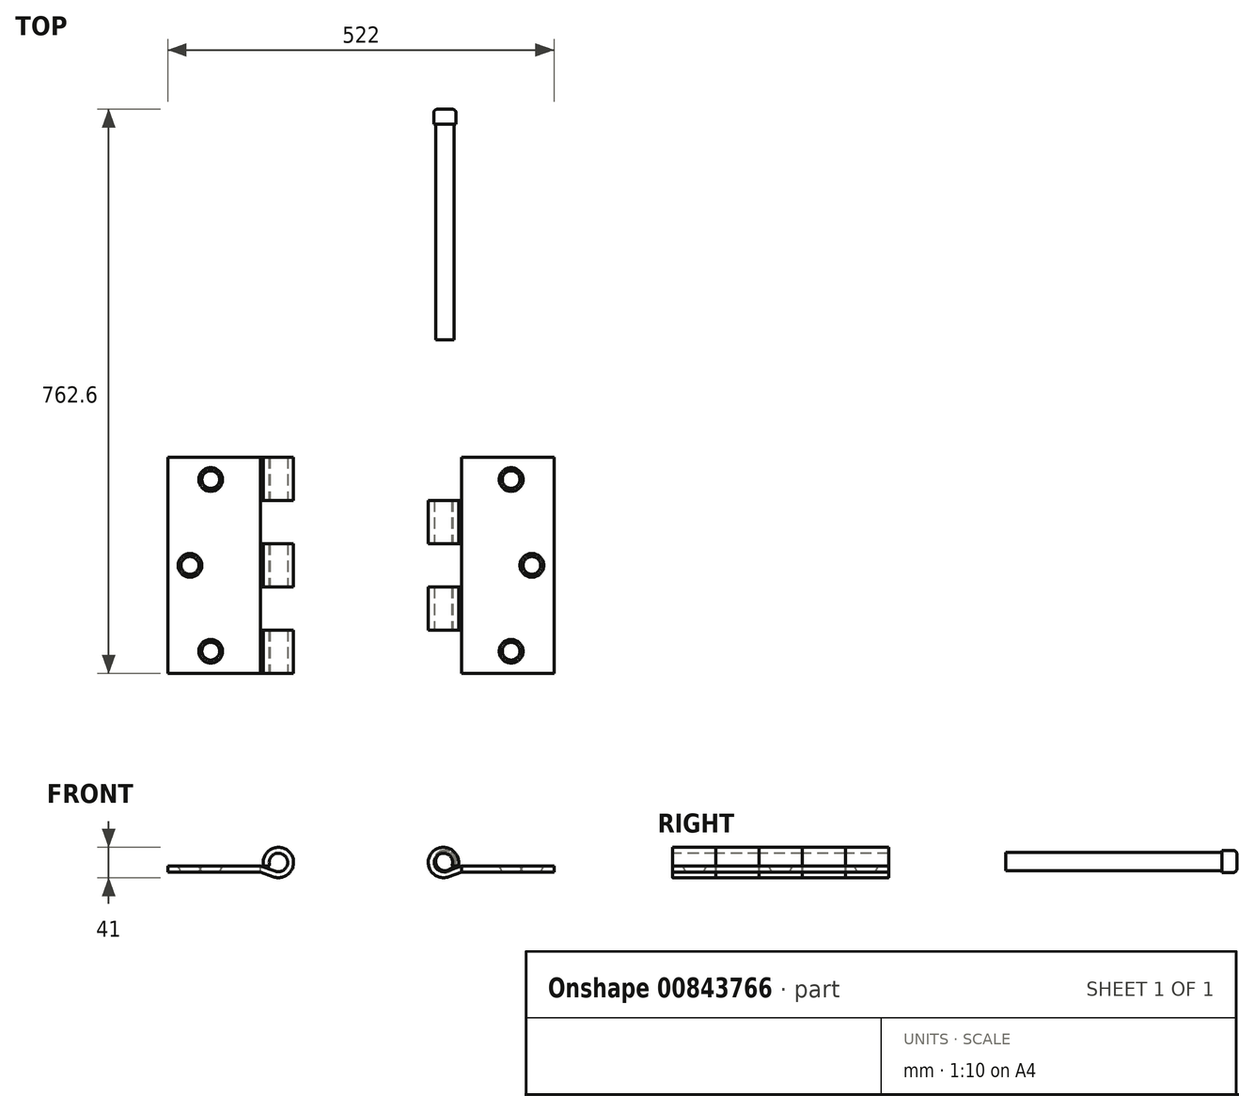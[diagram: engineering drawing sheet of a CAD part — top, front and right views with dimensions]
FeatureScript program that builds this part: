
annotation { "Feature Type Name" : "Feature", "Feature Type Description" : "" }
export const myFeature = defineFeature(function(context is Context, id is Id, definition is map)
    precondition{}
    {
        {
            var Q0;
            Q0=qCreatedBy(makeId("Top.planeOp"),FACE);
            var sketch = newSketch(context, id + "F0", { "sketchPlane" : qUnion([Q0])});
            skLineSegment(sketch, "E0.bottom", {"start": v(62.5, -146) * mm, "end": v(-62.5, -146) * mm});
            skLineSegment(sketch, "E0.top", {"start": v(62.5, 146) * mm, "end": v(-62.5, 146) * mm});
            skLineSegment(sketch, "E0.left", {"start": v(62.5, -146) * mm, "end": v(62.5, 146) * mm});
            skLineSegment(sketch, "E0.right", {"start": v(-62.5, -146) * mm, "end": v(-62.5, 146) * mm});
            skPoint(sketch, "E0.middle", {"position": v(0, 0) * mm});
            skLineSegment(sketch, "E1.bottom", {"start": v(62.5, 146) * mm, "end": v(4.5, 146) * mm});
            skLineSegment(sketch, "E1.left", {"start": v(62.5, 146) * mm, "end": v(62.5, 116) * mm});
            skLineSegment(sketch, "E2.bottom", {"start": v(62.5, -146) * mm, "end": v(4.5, -146) * mm});
            skSolve(sketch);
        }
        {
            var Q0;
            Q0=makeQuery(id+"F0.imprint","IMPRINT",FACE,{"disambiguationData":[TD([[makeQuery(id+"F0.imprint","IMPRINT",EDGE,{"derivedFrom":sQuery(id+"F0.wireOp",EDGE,"E0.bottom")}),-1.0]])]});
            extrude(context, id + "F1", {"entities" : qUnion([Q0]), "depth" : 8 * mm, "offsetDistance" : 25 * mm});
        }
        {
            var Q0;
            Q0=makeQuery(id+"F1.opExtrude","SWEPT_FACE",FACE,{"disambiguationData":[OSD([sQuery(id+"F0.wireOp",EDGE,"E0.right")])]});
            cPlane(context, id + "F2", {"entities" : qUnion([Q0]), "cplaneType" : CPlaneType.OFFSET, "offset" : 136 * mm, "width" : 150 * mm, "height" : 150 * mm});
        }
        {
            var Q0;
            Q0=makeQuery(id+"F1.opExtrude","SWEPT_FACE",FACE,{"disambiguationData":[OSD([sQuery(id+"F0.wireOp",EDGE,"E0.bottom"),sQuery(id+"F0.wireOp",EDGE,"E2.bottom")])]});
            var sketch = newSketch(context, id + "F3", { "sketchPlane" : qUnion([Q0])});
            skArc(sketch, "E3", {"start": v(-75.54, 8) * mm, "mid": v(-95.44, 22.22) * mm, "end": v(-83.04, 1.14) * mm});
            skArc(sketch, "E4", {"start": v(-67.12, 8) * mm, "mid": v(-102.19, 26.77) * mm, "end": v(-80.09, -6.3) * mm});
            skLineSegment(sketch, "E5", {"start": v(-62.5, 0) * mm, "end": v(-80.09, -6.3) * mm});
            skLineSegment(sketch, "E6", {"start": v(-62.5, 8) * mm, "end": v(-83.04, 1.14) * mm});
            skLineSegment(sketch, "E7", {"start": v(-67.12, 8) * mm, "end": v(-75.54, 8) * mm});
            skSolve(sketch);
        }
        {
            var Q0;
            Q0=makeQuery(id+"F3.imprint","IMPRINT",FACE,{"disambiguationData":[TD([[makeQuery(id+"F3.imprint","IMPRINT",EDGE,{"derivedFrom":sQuery(id+"F3.wireOp",EDGE,"E3")}),-1.0]])]});
            extrude(context, id + "F4", {"entities" : qUnion([Q0]), "operationType" : NewBodyOperationType.ADD, "oppositeDirection" : true, "depth" : 292 * mm, "offsetDistance" : 25 * mm});
        }
        {
            var Q0;
            Q0=makeQuery(id+"F1.opExtrude","CAP_FACE",FACE,{"disambiguationData":[OSD([sQuery(id+"F0.wireOp",EDGE,"E0.bottom"),sQuery(id+"F0.wireOp",EDGE,"E0.top"),sQuery(id+"F0.wireOp",EDGE,"E0.left"),sQuery(id+"F0.wireOp",EDGE,"E0.right"),sQuery(id+"F0.wireOp",EDGE,"E1.bottom"),sQuery(id+"F0.wireOp",EDGE,"E1.left"),sQuery(id+"F0.wireOp",EDGE,"E2.bottom")])],"isStart":false});
            var sketch = newSketch(context, id + "F5", { "sketchPlane" : qUnion([Q0])});
            skPoint(sketch, "E8.orphan", {"position": v(62.5, 0) * mm});
            skCircle(sketch, "E9", {"center": v(4.5, 116) * mm, "radius": 16 * mm});
            skCircle(sketch, "E10", {"center": v(32.5, 0) * mm, "radius": 16 * mm});
            skCircle(sketch, "E11", {"center": v(4.5, -116) * mm, "radius": 16 * mm});
            skSolve(sketch);
        }
        {
            var Q0;
            Q0=makeQuery(id+"F0.imprint","IMPRINT",FACE,{"disambiguationData":[TD([[makeQuery(id+"F0.imprint","IMPRINT",EDGE,{"derivedFrom":sQuery(id+"F0.wireOp",EDGE,"E0.bottom")}),-1.0]])]});
            var sketch = newSketch(context, id + "F6", { "sketchPlane" : qUnion([Q0])});
            skPoint(sketch, "E12.0", {"position": v(4.5, -116) * mm});
            skPoint(sketch, "E13.0", {"position": v(32.5, 0) * mm});
            skPoint(sketch, "E14.0", {"position": v(4.5, 116) * mm});
            skCircle(sketch, "E15", {"center": v(32.5, 0) * mm, "radius": 12 * mm});
            skCircle(sketch, "E16", {"center": v(4.5, -116) * mm, "radius": 12 * mm});
            skCircle(sketch, "E17", {"center": v(4.5, 116) * mm, "radius": 12 * mm});
            skSolve(sketch);
        }
        {
            var Q0;
            Q0=makeQuery(id+"F1.opExtrude","CAP_FACE",FACE,{"disambiguationData":[OSD([sQuery(id+"F0.wireOp",EDGE,"E0.bottom"),sQuery(id+"F0.wireOp",EDGE,"E0.top"),sQuery(id+"F0.wireOp",EDGE,"E0.left"),sQuery(id+"F0.wireOp",EDGE,"E0.right"),sQuery(id+"F0.wireOp",EDGE,"E1.bottom"),sQuery(id+"F0.wireOp",EDGE,"E1.left"),sQuery(id+"F0.wireOp",EDGE,"E2.bottom")])],"isStart":false});
            var sketch = newSketch(context, id + "F7", { "sketchPlane" : qUnion([Q0])});
            skLineSegment(sketch, "E18.bottom", {"start": v(-62.5, 146) * mm, "end": v(-181.75, 146) * mm});
            skLineSegment(sketch, "E18.top", {"start": v(-62.5, 87.6) * mm, "end": v(-181.75, 87.6) * mm});
            skLineSegment(sketch, "E18.left", {"start": v(-62.5, 146) * mm, "end": v(-62.5, 87.6) * mm});
            skLineSegment(sketch, "E18.right", {"start": v(-181.75, 146) * mm, "end": v(-181.75, 87.6) * mm});
            skLineSegment(sketch, "E19.bottom", {"start": v(-62.5, 29.2) * mm, "end": v(-181.75, 29.2) * mm});
            skLineSegment(sketch, "E19.top", {"start": v(-62.5, -29.2) * mm, "end": v(-181.75, -29.2) * mm});
            skLineSegment(sketch, "E19.left", {"start": v(-62.5, 29.2) * mm, "end": v(-62.5, -29.2) * mm});
            skLineSegment(sketch, "E19.right", {"start": v(-181.75, 29.2) * mm, "end": v(-181.75, -29.2) * mm});
            skLineSegment(sketch, "E20.bottom", {"start": v(-62.5, -87.6) * mm, "end": v(-181.74, -87.6) * mm});
            skLineSegment(sketch, "E20.top", {"start": v(-62.5, -146) * mm, "end": v(-181.74, -146) * mm});
            skLineSegment(sketch, "E20.left", {"start": v(-62.5, -87.6) * mm, "end": v(-62.5, -146) * mm});
            skLineSegment(sketch, "E20.right", {"start": v(-181.74, -87.6) * mm, "end": v(-181.74, -146) * mm});
            skSolve(sketch);
        }
        {
            var Q1;
            Q1=makeQuery(id+"F6.imprint","IMPRINT",FACE,{"disambiguationData":[TD([[makeQuery(id+"F6.imprint","IMPRINT",EDGE,{"derivedFrom":sQuery(id+"F6.wireOp",EDGE,"E16")}),1.0]])]});
            var Q2;
            Q2=makeQuery(id+"F5.imprint","IMPRINT",FACE,{"disambiguationData":[TD([[makeQuery(id+"F5.imprint","IMPRINT",EDGE,{"derivedFrom":sQuery(id+"F5.wireOp",EDGE,"E11")}),1.0]])]});
            loft(context, id + "F8", {"operationType" : NewBodyOperationType.REMOVE, "sheetProfilesArray" : [{ "sheetProfileEntities" : qUnion([Q1]) }, { "sheetProfileEntities" : qUnion([Q2]) }]});
        }
        {
            var Q1;
            Q1=makeQuery(id+"F6.imprint","IMPRINT",FACE,{"disambiguationData":[TD([[makeQuery(id+"F6.imprint","IMPRINT",EDGE,{"derivedFrom":sQuery(id+"F6.wireOp",EDGE,"E15")}),1.0]])]});
            var Q2;
            Q2=makeQuery(id+"F5.imprint","IMPRINT",FACE,{"disambiguationData":[TD([[makeQuery(id+"F5.imprint","IMPRINT",EDGE,{"derivedFrom":sQuery(id+"F5.wireOp",EDGE,"E10")}),1.0]])]});
            loft(context, id + "F9", {"operationType" : NewBodyOperationType.REMOVE, "sheetProfilesArray" : [{ "sheetProfileEntities" : qUnion([Q1]) }, { "sheetProfileEntities" : qUnion([Q2]) }]});
        }
        {
            var Q1;
            Q1=makeQuery(id+"F5.imprint","IMPRINT",FACE,{"disambiguationData":[TD([[makeQuery(id+"F5.imprint","IMPRINT",EDGE,{"derivedFrom":sQuery(id+"F5.wireOp",EDGE,"E9")}),1.0]])]});
            var Q2;
            Q2=makeQuery(id+"F6.imprint","IMPRINT",FACE,{"disambiguationData":[TD([[makeQuery(id+"F6.imprint","IMPRINT",EDGE,{"derivedFrom":sQuery(id+"F6.wireOp",EDGE,"E17")}),1.0]])]});
            loft(context, id + "F10", {"operationType" : NewBodyOperationType.REMOVE, "sheetProfilesArray" : [{ "sheetProfileEntities" : qUnion([Q1]) }, { "sheetProfileEntities" : qUnion([Q2]) }]});
        }
        {
            var Q0;
            Q0=makeQuery(id+"F1.opExtrude","SWEPT_BODY",BODY,{"disambiguationData":[OSD([sQuery(id+"F0.wireOp",EDGE,"E0.bottom"),sQuery(id+"F0.wireOp",EDGE,"E0.top"),sQuery(id+"F0.wireOp",EDGE,"E0.left"),sQuery(id+"F0.wireOp",EDGE,"E0.right"),sQuery(id+"F0.wireOp",EDGE,"E1.bottom"),sQuery(id+"F0.wireOp",EDGE,"E1.left"),sQuery(id+"F0.wireOp",EDGE,"E2.bottom")])]});
            var Q1;
            Q1=qCreatedBy(id+"F2.planeOp",FACE);
            mirror(context, id + "F11", {"entities" : qUnion([Q0]), "mirrorPlane" : qUnion([Q1])});
        }
        {
            var Q0;
            Q0=makeQuery(id+"F11.opPattern","COPY",FACE,{"derivedFrom":makeQuery(id+"F1.opExtrude","CAP_FACE",FACE,{"disambiguationData":[OSD([sQuery(id+"F0.wireOp",EDGE,"E0.bottom"),sQuery(id+"F0.wireOp",EDGE,"E0.top"),sQuery(id+"F0.wireOp",EDGE,"E0.left"),sQuery(id+"F0.wireOp",EDGE,"E0.right"),sQuery(id+"F0.wireOp",EDGE,"E1.bottom"),sQuery(id+"F0.wireOp",EDGE,"E1.left"),sQuery(id+"F0.wireOp",EDGE,"E2.bottom")])],"isStart":false}),"instanceName":"1"});
            var sketch = newSketch(context, id + "F12", { "sketchPlane" : qUnion([Q0])});
            skLineSegment(sketch, "E21.bottom", {"start": v(-334.5, -87.6) * mm, "end": v(-219.8, -87.6) * mm});
            skLineSegment(sketch, "E21.top", {"start": v(-334.5, -29.2) * mm, "end": v(-219.8, -29.2) * mm});
            skLineSegment(sketch, "E21.left", {"start": v(-334.5, -87.6) * mm, "end": v(-334.5, -29.2) * mm});
            skLineSegment(sketch, "E21.right", {"start": v(-219.8, -87.6) * mm, "end": v(-219.8, -29.2) * mm});
            skLineSegment(sketch, "E22.bottom", {"start": v(-334.5, 87.6) * mm, "end": v(-219.8, 87.6) * mm});
            skLineSegment(sketch, "E22.top", {"start": v(-334.5, 29.2) * mm, "end": v(-219.8, 29.2) * mm});
            skLineSegment(sketch, "E22.left", {"start": v(-334.5, 87.6) * mm, "end": v(-334.5, 29.2) * mm});
            skLineSegment(sketch, "E22.right", {"start": v(-219.8, 87.6) * mm, "end": v(-219.8, 29.2) * mm});
            skSolve(sketch);
        }
        {
            var Q0;
            Q0=makeQuery(id+"F12.imprint","IMPRINT",FACE,{"disambiguationData":[TD([[makeQuery(id+"F12.imprint","IMPRINT",EDGE,{"derivedFrom":sQuery(id+"F12.wireOp",EDGE,"E21.bottom")}),1.0]])]});
            var Q1;
            Q1=makeQuery(id+"F12.imprint","IMPRINT",FACE,{"disambiguationData":[TD([[makeQuery(id+"F12.imprint","IMPRINT",EDGE,{"derivedFrom":sQuery(id+"F12.wireOp",EDGE,"E22.bottom")}),-1.0]])]});
            var Q2;
            Q2=makeQuery(id+"F7.imprint","IMPRINT",FACE,{"disambiguationData":[TD([[makeQuery(id+"F7.imprint","IMPRINT",EDGE,{"derivedFrom":sQuery(id+"F7.wireOp",EDGE,"E19.bottom")}),1.0]])]});
            var Q3;
            Q3=makeQuery(id+"F7.imprint","IMPRINT",FACE,{"disambiguationData":[TD([[makeQuery(id+"F7.imprint","IMPRINT",EDGE,{"derivedFrom":sQuery(id+"F7.wireOp",EDGE,"E18.bottom")}),1.0]])]});
            var Q4;
            Q4=makeQuery(id+"F7.imprint","IMPRINT",FACE,{"disambiguationData":[TD([[makeQuery(id+"F7.imprint","IMPRINT",EDGE,{"derivedFrom":sQuery(id+"F7.wireOp",EDGE,"E20.bottom")}),1.0]])]});
            extrude(context, id + "F13", {"entities" : qUnion([Q0, Q1, Q2, Q3, Q4]), "operationType" : NewBodyOperationType.REMOVE, "endBound" : BoundingType.SYMMETRIC, "oppositeDirection" : true, "depth" : 100 * mm, "offsetDistance" : 25 * mm});
        }
        {
            var Q0;
            Q0=makeQuery(id+"F13.boolean.opBoolean","COPY",FACE,{"derivedFrom":makeQuery(id+"F13.opExtrude","SWEPT_FACE",FACE,{"disambiguationData":[OSD([sQuery(id+"F7.wireOp",EDGE,"E18.top")])]})});
            cPlane(context, id + "F14", {"entities" : qUnion([Q0]), "cplaneType" : CPlaneType.OFFSET, "offset" : 217 * mm, "width" : 150 * mm, "height" : 150 * mm});
        }
        {
            var Q0;
            Q0=qCreatedBy(id+"F14.planeOp",FACE);
            var sketch = newSketch(context, id + "F15", { "sketchPlane" : qUnion([Q0])});
            skCircle(sketch, "E23", {"center": v(85.03, 14.37) * mm, "radius": 12.5 * mm});
            skSolve(sketch);
        }
        {
            var Q0;
            Q0=makeQuery(id+"F15.imprint","IMPRINT",FACE,{"disambiguationData":[TD([[makeQuery(id+"F15.imprint","IMPRINT",EDGE,{"derivedFrom":sQuery(id+"F15.wireOp",EDGE,"E23")}),1.0]])]});
            extrude(context, id + "F16", {"entities" : qUnion([Q0]), "depth" : 292 * mm, "offsetDistance" : 25 * mm});
        }
        {
            var Q0;
            Q0=makeQuery(id+"F16.opExtrude","CAP_FACE",FACE,{"disambiguationData":[OSD([sQuery(id+"F15.wireOp",EDGE,"E23")])],"isStart":false});
            var sketch = newSketch(context, id + "F17", { "sketchPlane" : qUnion([Q0])});
            skCircle(sketch, "E24", {"center": v(85.03, 14.37) * mm, "radius": 15 * mm});
            skSolve(sketch);
        }
        {
            var Q0;
            Q0=makeQuery(id+"F17.imprint","IMPRINT",FACE,{"disambiguationData":[TD([[makeQuery(id+"F17.imprint","IMPRINT",EDGE,{"derivedFrom":makeQuery(id+"F16.opExtrude","CAP_EDGE",EDGE,{"disambiguationData":[OSD([sQuery(id+"F15.wireOp",EDGE,"E23")])],"isStart":false})}),1.0]])]});
            var Q1;
            Q1=makeQuery(id+"F17.imprint","IMPRINT",FACE,{"disambiguationData":[TD([[makeQuery(id+"F17.imprint","IMPRINT",EDGE,{"derivedFrom":sQuery(id+"F17.wireOp",EDGE,"E24")}),1.0]])]});
            extrude(context, id + "F18", {"entities" : qUnion([Q0, Q1]), "operationType" : NewBodyOperationType.ADD, "depth" : 20 * mm, "offsetDistance" : 25 * mm});
        }
        {
            var Q0;
            Q0=makeQuery(id+"F18.opExtrude","CAP_FACE",FACE,{"disambiguationData":[OSD([sQuery(id+"F17.wireOp",EDGE,"E24")])],"isStart":false});
            fillet(context, id + "F19", {"entities" : qUnion([Q0]), "radius" : 5 * mm, "tangentPropagation" : true, "allowEdgeOverflow" : false});
        }
    });
